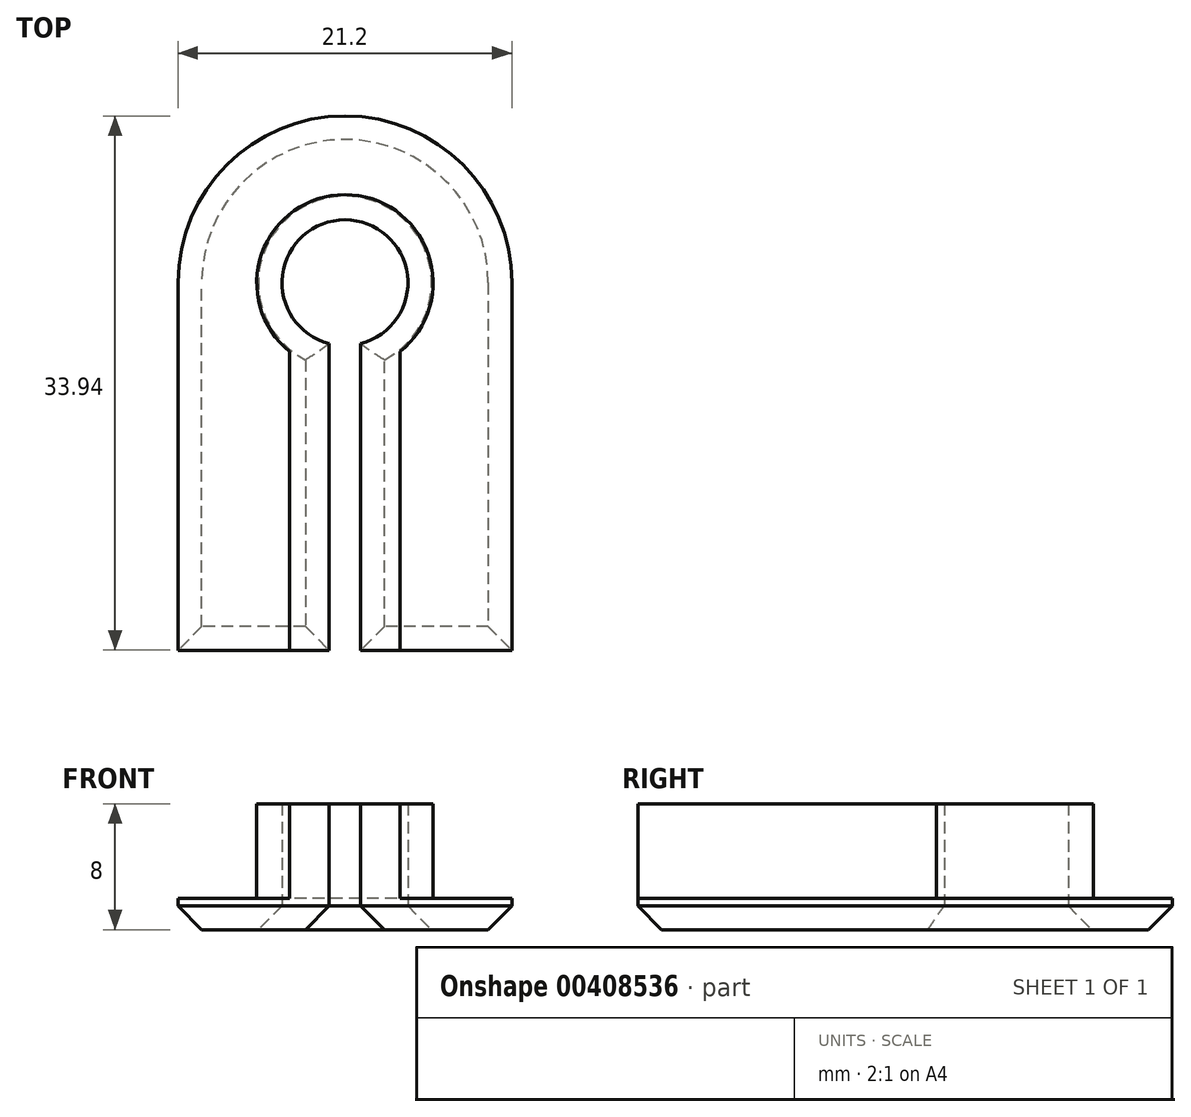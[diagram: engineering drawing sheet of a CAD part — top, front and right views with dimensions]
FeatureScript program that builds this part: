
annotation { "Feature Type Name" : "Feature", "Feature Type Description" : "" }
export const myFeature = defineFeature(function(context is Context, id is Id, definition is map)
    precondition{}
    {
        {
            var Q0;
            Q0=qCreatedBy(makeId("Top.planeOp"),FACE);
            var sketch = newSketch(context, id + "F0", { "sketchPlane" : qUnion([Q0])});
            skCircle(sketch, "E0", {"center": v(0, 0) * mm, "radius": 4 * mm});
            skCircle(sketch, "E1.0", {"center": v(0, 0) * mm, "radius": 5.6 * mm});
            skCircle(sketch, "E2.0", {"center": v(0, 0) * mm, "radius": 10.6 * mm});
            skLineSegment(sketch, "E3", {"start": v(-10.6, 0) * mm, "end": v(-10.6, -23.34) * mm});
            skLineSegment(sketch, "E4", {"start": v(-10.6, -23.34) * mm, "end": v(10.6, -23.34) * mm});
            skLineSegment(sketch, "E5", {"start": v(10.6, -23.34) * mm, "end": v(10.6, 0) * mm});
            skLineSegment(sketch, "E6.bottom", {"start": v(-1, -23.34) * mm, "end": v(1, -23.34) * mm});
            skLineSegment(sketch, "E6.top", {"start": v(-1, -2.55) * mm, "end": v(1, -2.55) * mm});
            skLineSegment(sketch, "E6.left", {"start": v(-1, -23.34) * mm, "end": v(-1, -2.55) * mm});
            skLineSegment(sketch, "E6.right", {"start": v(1, -23.34) * mm, "end": v(1, -2.55) * mm});
            skLineSegment(sketch, "E7", {"start": v(-3.5, -1.94) * mm, "end": v(-3.5, -23.34) * mm});
            skLineSegment(sketch, "E8", {"start": v(-3.5, -23.34) * mm, "end": v(3.5, -23.34) * mm});
            skLineSegment(sketch, "E9", {"start": v(3.5, -23.34) * mm, "end": v(3.5, -1.94) * mm});
            skSolve(sketch);
        }
        {
            var Q0;
            {var subQ0=sQuery(id+"F0.wireOp",EDGE,"E3");Q0=makeQuery(id+"F0.imprint","IMPRINT",FACE,{"disambiguationData":[TD([[makeQuery(id+"F0.imprint","IMPRINT",EDGE,{"derivedFrom":subQ0}),1.0]])]});}
            var Q1;
            {var subQ0=sQuery(id+"F0.wireOp",EDGE,"E5");Q1=makeQuery(id+"F0.imprint","IMPRINT",FACE,{"disambiguationData":[TD([[makeQuery(id+"F0.imprint","IMPRINT",EDGE,{"derivedFrom":subQ0}),1.0]])]});}
            var Q2;
            {var subQ0=sQuery(id+"F0.wireOp",EDGE,"E6.right");var subQ1=sQuery(id+"F0.wireOp",EDGE,"E2.0");var subQ2=makeQuery(id+"F0.imprint","INTERSECT",VERTEX,{"derivedFrom":[subQ1,subQ0]});Q2=makeQuery(id+"F0.imprint","IMPRINT",FACE,{"disambiguationData":[TD([[makeQuery(id+"F0.imprint","IMPRINT",EDGE,{"disambiguationData":[TD([[subQ2,-1.0]])],"derivedFrom":subQ1}),-1.0]])]});}
            var Q3;
            {var subQ0=sQuery(id+"F0.wireOp",EDGE,"E7");var subQ1=sQuery(id+"F0.wireOp",EDGE,"E2.0");var subQ2=makeQuery(id+"F0.imprint","INTERSECT",VERTEX,{"derivedFrom":[subQ1,subQ0]});Q3=makeQuery(id+"F0.imprint","IMPRINT",FACE,{"disambiguationData":[TD([[makeQuery(id+"F0.imprint","IMPRINT",EDGE,{"disambiguationData":[TD([[subQ2,-1.0]])],"derivedFrom":subQ1}),-1.0]])]});}
            var Q4;
            {var subQ0=sQuery(id+"F0.wireOp",EDGE,"E6.left");var subQ1=sQuery(id+"F0.wireOp",EDGE,"E1.0");var subQ2=makeQuery(id+"F0.imprint","INTERSECT",VERTEX,{"derivedFrom":[subQ1,subQ0]});Q4=makeQuery(id+"F0.imprint","IMPRINT",FACE,{"disambiguationData":[TD([[makeQuery(id+"F0.imprint","IMPRINT",EDGE,{"disambiguationData":[TD([[subQ2,1.0]])],"derivedFrom":subQ1}),-1.0]])]});}
            var Q5;
            {var subQ2=sQuery(id+"F0.wireOp",EDGE,"E7");var subQ7=sQuery(id+"F0.wireOp",EDGE,"E1.0");var subQ8=makeQuery(id+"F0.imprint","INTERSECT",VERTEX,{"derivedFrom":[subQ7,subQ2]});Q5=makeQuery(id+"F0.imprint","IMPRINT",FACE,{"disambiguationData":[TD([[makeQuery(id+"F0.imprint","IMPRINT",EDGE,{"disambiguationData":[TD([[subQ8,1.0]])],"derivedFrom":subQ7}),-1.0]])]});}
            var Q6;
            {var subQ0=sQuery(id+"F0.wireOp",EDGE,"E7");var subQ1=sQuery(id+"F0.wireOp",EDGE,"E0");var subQ2=makeQuery(id+"F0.imprint","INTERSECT",VERTEX,{"derivedFrom":[subQ1,subQ0]});Q6=makeQuery(id+"F0.imprint","IMPRINT",FACE,{"disambiguationData":[TD([[makeQuery(id+"F0.imprint","IMPRINT",EDGE,{"disambiguationData":[TD([[subQ2,1.0]])],"derivedFrom":subQ1}),-1.0]])]});}
            var Q7;
            {var subQ0=sQuery(id+"F0.wireOp",EDGE,"E6.right");var subQ1=sQuery(id+"F0.wireOp",EDGE,"E1.0");var subQ2=makeQuery(id+"F0.imprint","INTERSECT",VERTEX,{"derivedFrom":[subQ1,subQ0]});Q7=makeQuery(id+"F0.imprint","IMPRINT",FACE,{"disambiguationData":[TD([[makeQuery(id+"F0.imprint","IMPRINT",EDGE,{"disambiguationData":[TD([[subQ2,-1.0]])],"derivedFrom":subQ1}),-1.0]])]});}
            var Q8;
            {var subQ0=sQuery(id+"F0.wireOp",EDGE,"E9");var subQ1=sQuery(id+"F0.wireOp",EDGE,"E0");var subQ2=makeQuery(id+"F0.imprint","INTERSECT",VERTEX,{"derivedFrom":[subQ1,subQ0]});Q8=makeQuery(id+"F0.imprint","IMPRINT",FACE,{"disambiguationData":[TD([[makeQuery(id+"F0.imprint","IMPRINT",EDGE,{"disambiguationData":[TD([[subQ2,1.0]])],"derivedFrom":subQ1}),-1.0]])]});}
            var Q9;
            {var subQ0=sQuery(id+"F0.wireOp",EDGE,"E7");var subQ1=sQuery(id+"F0.wireOp",EDGE,"E0");var subQ2=makeQuery(id+"F0.imprint","INTERSECT",VERTEX,{"derivedFrom":[subQ1,subQ0]});Q9=makeQuery(id+"F0.imprint","IMPRINT",FACE,{"disambiguationData":[TD([[makeQuery(id+"F0.imprint","IMPRINT",EDGE,{"disambiguationData":[TD([[subQ2,-1.0]])],"derivedFrom":subQ1}),-1.0]])]});}
            extrude(context, id + "F1", {"entities" : qUnion([Q0, Q1, Q2, Q3, Q4, Q5, Q6, Q7, Q8, Q9]), "depth" : 2 * mm});
        }
        {
            var Q0;
            {var subQ0=sQuery(id+"F0.wireOp",EDGE,"E7");var subQ1=sQuery(id+"F0.wireOp",EDGE,"E0");var subQ2=makeQuery(id+"F0.imprint","INTERSECT",VERTEX,{"derivedFrom":[subQ1,subQ0]});Q0=makeQuery(id+"F0.imprint","IMPRINT",FACE,{"disambiguationData":[TD([[makeQuery(id+"F0.imprint","IMPRINT",EDGE,{"disambiguationData":[TD([[subQ2,1.0]])],"derivedFrom":subQ1}),-1.0]])]});}
            var Q1;
            {var subQ0=sQuery(id+"F0.wireOp",EDGE,"E6.left");var subQ1=sQuery(id+"F0.wireOp",EDGE,"E1.0");var subQ2=makeQuery(id+"F0.imprint","INTERSECT",VERTEX,{"derivedFrom":[subQ1,subQ0]});Q1=makeQuery(id+"F0.imprint","IMPRINT",FACE,{"disambiguationData":[TD([[makeQuery(id+"F0.imprint","IMPRINT",EDGE,{"disambiguationData":[TD([[subQ2,1.0]])],"derivedFrom":subQ1}),-1.0]])]});}
            var Q2;
            {var subQ0=sQuery(id+"F0.wireOp",EDGE,"E7");var subQ1=sQuery(id+"F0.wireOp",EDGE,"E2.0");var subQ2=makeQuery(id+"F0.imprint","INTERSECT",VERTEX,{"derivedFrom":[subQ1,subQ0]});Q2=makeQuery(id+"F0.imprint","IMPRINT",FACE,{"disambiguationData":[TD([[makeQuery(id+"F0.imprint","IMPRINT",EDGE,{"disambiguationData":[TD([[subQ2,-1.0]])],"derivedFrom":subQ1}),-1.0]])]});}
            var Q3;
            {var subQ0=sQuery(id+"F0.wireOp",EDGE,"E6.right");var subQ1=sQuery(id+"F0.wireOp",EDGE,"E2.0");var subQ2=makeQuery(id+"F0.imprint","INTERSECT",VERTEX,{"derivedFrom":[subQ1,subQ0]});Q3=makeQuery(id+"F0.imprint","IMPRINT",FACE,{"disambiguationData":[TD([[makeQuery(id+"F0.imprint","IMPRINT",EDGE,{"disambiguationData":[TD([[subQ2,-1.0]])],"derivedFrom":subQ1}),-1.0]])]});}
            var Q4;
            {var subQ0=sQuery(id+"F0.wireOp",EDGE,"E6.right");var subQ1=sQuery(id+"F0.wireOp",EDGE,"E1.0");var subQ2=makeQuery(id+"F0.imprint","INTERSECT",VERTEX,{"derivedFrom":[subQ1,subQ0]});Q4=makeQuery(id+"F0.imprint","IMPRINT",FACE,{"disambiguationData":[TD([[makeQuery(id+"F0.imprint","IMPRINT",EDGE,{"disambiguationData":[TD([[subQ2,-1.0]])],"derivedFrom":subQ1}),-1.0]])]});}
            var Q5;
            {var subQ0=sQuery(id+"F0.wireOp",EDGE,"E9");var subQ1=sQuery(id+"F0.wireOp",EDGE,"E0");var subQ2=makeQuery(id+"F0.imprint","INTERSECT",VERTEX,{"derivedFrom":[subQ1,subQ0]});Q5=makeQuery(id+"F0.imprint","IMPRINT",FACE,{"disambiguationData":[TD([[makeQuery(id+"F0.imprint","IMPRINT",EDGE,{"disambiguationData":[TD([[subQ2,1.0]])],"derivedFrom":subQ1}),-1.0]])]});}
            var Q6;
            {var subQ0=sQuery(id+"F0.wireOp",EDGE,"E7");var subQ1=sQuery(id+"F0.wireOp",EDGE,"E0");var subQ2=makeQuery(id+"F0.imprint","INTERSECT",VERTEX,{"derivedFrom":[subQ1,subQ0]});Q6=makeQuery(id+"F0.imprint","IMPRINT",FACE,{"disambiguationData":[TD([[makeQuery(id+"F0.imprint","IMPRINT",EDGE,{"disambiguationData":[TD([[subQ2,-1.0]])],"derivedFrom":subQ1}),-1.0]])]});}
            extrude(context, id + "F2", {"entities" : qUnion([Q0, Q1, Q2, Q3, Q4, Q5, Q6]), "operationType" : NewBodyOperationType.ADD, "depth" : 8 * mm});
        }
        {
            var Q0;
            Q0=makeQuery(id+"F1.opExtrude","CAP_FACE",FACE,{"disambiguationData":[OSD([sQuery(id+"F0.wireOp",EDGE,"E0"),sQuery(id+"F0.wireOp",EDGE,"E2.0"),sQuery(id+"F0.wireOp",EDGE,"E3"),sQuery(id+"F0.wireOp",EDGE,"E4"),sQuery(id+"F0.wireOp",EDGE,"E5"),sQuery(id+"F0.wireOp",EDGE,"E6.left"),sQuery(id+"F0.wireOp",EDGE,"E6.right"),sQuery(id+"F0.wireOp",EDGE,"E8")])],"isStart":true});
            chamfer(context, id + "F3", {"entities" : qUnion([Q0]), "width" : 1.5 * mm, "tangentPropagation" : true});
        }
    });
